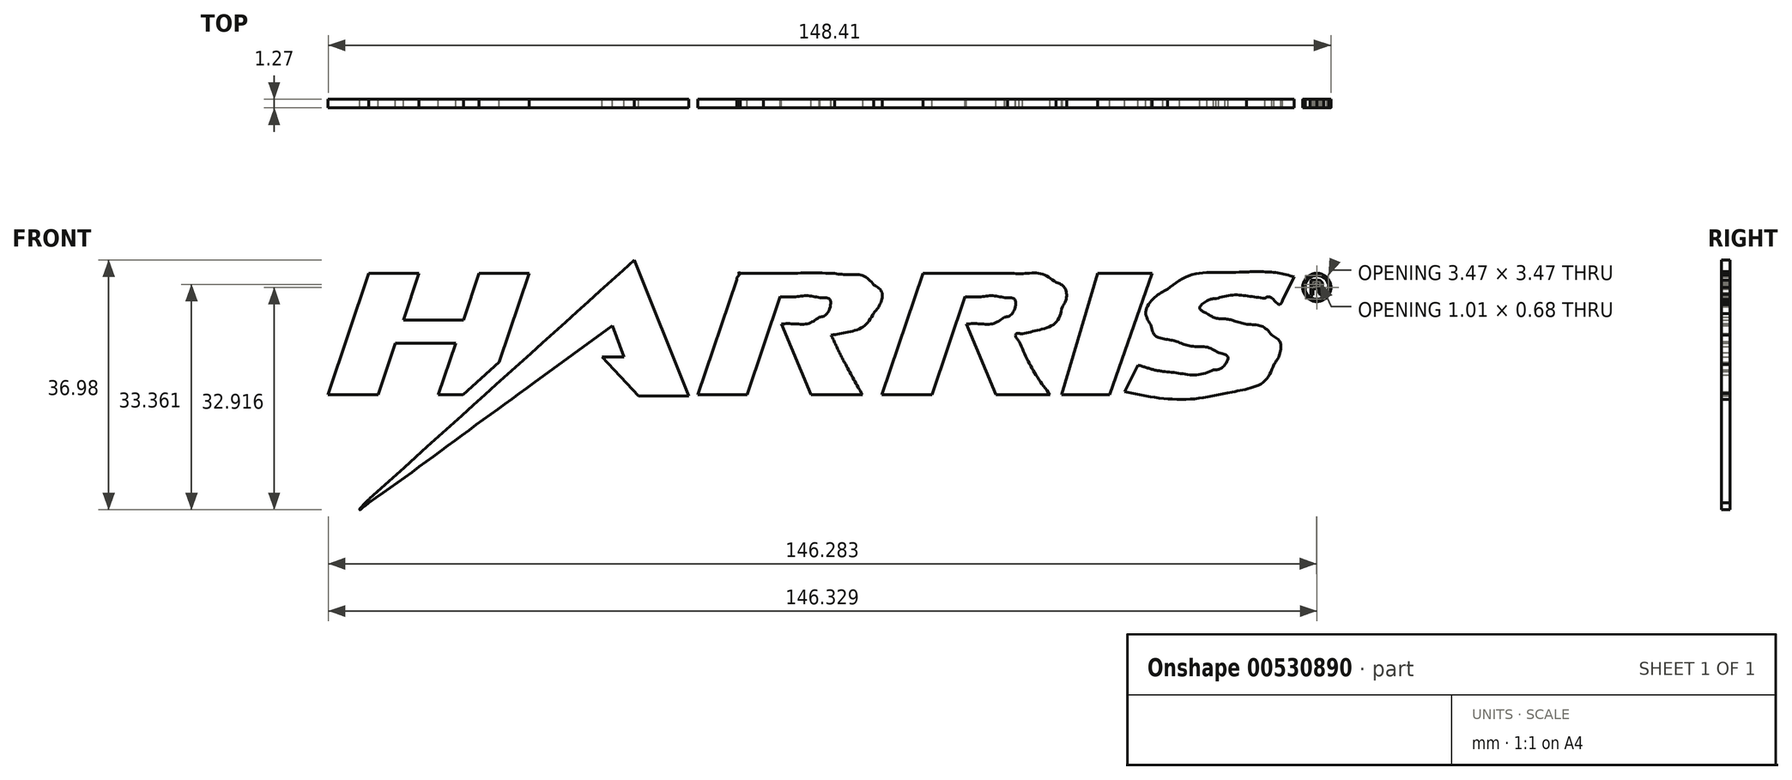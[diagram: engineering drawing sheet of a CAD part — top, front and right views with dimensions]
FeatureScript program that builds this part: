
annotation { "Feature Type Name" : "Feature", "Feature Type Description" : "" }
export const myFeature = defineFeature(function(context is Context, id is Id, definition is map)
    precondition{}
    {
        {
            var Q0;
            Q0=qCreatedBy(makeId("Front.planeOp"),FACE);
            var sketch = newSketch(context, id + "F0", { "sketchPlane" : qUnion([Q0])});
            skFitSpline(sketch, "E0", {"points": [v(63.7, 16.41) * mm, v(59.7, 16.31) * mm, v(55.5, 15.96) * mm, v(52, 13.85) * mm]});
            skFitSpline(sketch, "E1", {"points": [v(52, 13.85) * mm, v(50.3, 12.78) * mm, v(48.82, 10.63) * mm, v(49.53, 8.56) * mm]});
            skFitSpline(sketch, "E2", {"points": [v(49.53, 8.56) * mm, v(50.28, 6.91) * mm, v(52.2, 6.38) * mm, v(53.8, 5.94) * mm]});
            skFitSpline(sketch, "E3", {"points": [v(53.8, 5.94) * mm, v(55.72, 5.38) * mm, v(57.78, 5.29) * mm, v(59.6, 4.42) * mm]});
            skFitSpline(sketch, "E4", {"points": [v(59.6, 4.42) * mm, v(60.96, 3.78) * mm, v(60, 2.15) * mm, v(58.86, 1.94) * mm]});
            skFitSpline(sketch, "E5", {"points": [v(58.86, 1.94) * mm, v(56.44, 1.15) * mm, v(53.82, 1.39) * mm, v(51.33, 1.69) * mm]});
            skFitSpline(sketch, "E6", {"points": [v(51.33, 1.69) * mm, v(50.09, 1.9) * mm, v(48.87, 2.25) * mm, v(47.66, 2.62) * mm]});
            skFitSpline(sketch, "E7", {"points": [v(47.66, 2.62) * mm, v(47, 1.3) * mm, v(46.34, 0) * mm, v(45.68, -1.31) * mm]});
            skFitSpline(sketch, "E8", {"points": [v(45.68, -1.31) * mm, v(50.57, -2.22) * mm, v(55.62, -2.42) * mm, v(60.53, -1.59) * mm]});
            skFitSpline(sketch, "E9", {"points": [v(60.53, -1.59) * mm, v(63.32, -1.03) * mm, v(66.28, 0.15) * mm, v(67.78, 2.72) * mm]});
            skFitSpline(sketch, "E10", {"points": [v(67.78, 2.72) * mm, v(68.57, 4.04) * mm, v(68.7, 5.97) * mm, v(67.46, 7.06) * mm]});
            skFitSpline(sketch, "E11", {"points": [v(67.46, 7.06) * mm, v(65.98, 8.37) * mm, v(63.93, 8.64) * mm, v(62.08, 9.1) * mm]});
            skFitSpline(sketch, "E12", {"points": [v(62.08, 9.1) * mm, v(60.69, 9.44) * mm, v(59.2, 9.56) * mm, v(57.9, 10.22) * mm]});
            skFitSpline(sketch, "E13", {"points": [v(57.9, 10.22) * mm, v(56.8, 11.12) * mm, v(58.22, 12.3) * mm, v(59.2, 12.42) * mm]});
            skFitSpline(sketch, "E14", {"points": [v(59.2, 12.42) * mm, v(61.56, 12.98) * mm, v(64.04, 12.81) * mm, v(66.44, 12.5) * mm]});
            skFitSpline(sketch, "E15", {"points": [v(66.44, 12.5) * mm, v(67.26, 12.67) * mm, v(68.55, 11.58) * mm, v(69.06, 12.18) * mm]});
            skFitSpline(sketch, "E16", {"points": [v(69.06, 12.18) * mm, v(69.63, 13.34) * mm, v(70.2, 14.5) * mm, v(70.78, 15.68) * mm]});
            skFitSpline(sketch, "E17", {"points": [v(70.78, 15.68) * mm, v(68.47, 16.24) * mm, v(66.06, 16.43) * mm, v(63.7, 16.41) * mm]});
            skLineSegment(sketch, "E18", {"start": v(-66.17, 16.22) * mm, "end": v(-72.2, -1.78) * mm});
            skLineSegment(sketch, "E19", {"start": v(-72.2, -1.78) * mm, "end": v(-64.8, -1.78) * mm});
            skLineSegment(sketch, "E20", {"start": v(-64.8, -1.78) * mm, "end": v(-62.24, 5.84) * mm});
            skLineSegment(sketch, "E21", {"start": v(-62.24, 5.84) * mm, "end": v(-53.33, 5.84) * mm});
            skLineSegment(sketch, "E22", {"start": v(-53.33, 5.84) * mm, "end": v(-55.9, -1.78) * mm});
            skLineSegment(sketch, "E23", {"start": v(-55.9, -1.78) * mm, "end": v(-52.23, -1.78) * mm});
            skLineSegment(sketch, "E24", {"start": v(-52.23, -1.78) * mm, "end": v(-46.86, 3.06) * mm});
            skLineSegment(sketch, "E25", {"start": v(-46.86, 3.06) * mm, "end": v(-42.47, 16.22) * mm});
            skLineSegment(sketch, "E26", {"start": v(-42.47, 16.22) * mm, "end": v(-49.87, 16.22) * mm});
            skLineSegment(sketch, "E27", {"start": v(-49.87, 16.22) * mm, "end": v(-52.19, 9.3) * mm});
            skLineSegment(sketch, "E28", {"start": v(-52.19, 9.3) * mm, "end": v(-61.07, 9.3) * mm});
            skLineSegment(sketch, "E29", {"start": v(-61.07, 9.3) * mm, "end": v(-58.75, 16.22) * mm});
            skLineSegment(sketch, "E30", {"start": v(-58.75, 16.22) * mm, "end": v(-66.17, 16.22) * mm});
            skLineSegment(sketch, "E31", {"start": v(-70.17, 16.22) * mm, "end": v(-70.17, 16.22) * mm});
            skFitSpline(sketch, "E32", {"points": [v(4.38, 2.72) * mm, v(3.62, 4.13) * mm, v(2.93, 5.58) * mm, v(2.26, 7.04) * mm]});
            skFitSpline(sketch, "E33", {"points": [v(2.26, 7.04) * mm, v(4.58, 7.47) * mm, v(7.08, 8.34) * mm, v(8.54, 10.31) * mm]});
            skFitSpline(sketch, "E34", {"points": [v(8.54, 10.31) * mm, v(9.42, 11.5) * mm, v(9.75, 13.37) * mm, v(8.57, 14.48) * mm]});
            skFitSpline(sketch, "E35", {"points": [v(8.57, 14.48) * mm, v(6.98, 15.84) * mm, v(4.77, 16) * mm, v(2.78, 16.17) * mm]});
            skFitSpline(sketch, "E36", {"points": [v(2.78, 16.17) * mm, v(-0.74, 16.27) * mm, v(-4.26, 16.2) * mm, v(-7.77, 16.22) * mm]});
            skFitSpline(sketch, "E37", {"points": [v(-7.77, 16.22) * mm, v(-9.03, 16.22) * mm, v(-10.3, 16.22) * mm, v(-11.56, 16.22) * mm]});
            skFitSpline(sketch, "E38", {"points": [v(-11.56, 16.22) * mm, v(-11.19, 16.22) * mm, v(-11.7, 15.53) * mm, v(-11.72, 15.24) * mm]});
            skFitSpline(sketch, "E39", {"points": [v(-11.72, 15.24) * mm, v(-13.64, 9.58) * mm, v(-15.56, 3.9) * mm, v(-17.48, -1.76) * mm]});
            skFitSpline(sketch, "E40", {"points": [v(-17.48, -1.76) * mm, v(-15.05, -1.77) * mm, v(-12.62, -1.77) * mm, v(-10.2, -1.78) * mm]});
            skFitSpline(sketch, "E41", {"points": [v(-10.2, -1.78) * mm, v(-8.57, 3.07) * mm, v(-6.94, 7.9) * mm, v(-5.31, 12.75) * mm]});
            skFitSpline(sketch, "E42", {"points": [v(-5.31, 12.75) * mm, v(-3.35, 12.7) * mm, v(-1.37, 12.88) * mm, v(0.57, 12.56) * mm]});
            skFitSpline(sketch, "E43", {"points": [v(0.57, 12.56) * mm, v(2.09, 12.25) * mm, v(1.6, 10.2) * mm, v(0.48, 9.7) * mm]});
            skFitSpline(sketch, "E44", {"points": [v(0.48, 9.7) * mm, v(-1.22, 8.76) * mm, v(-3.24, 8.72) * mm, v(-5.14, 8.72) * mm]});
            skFitSpline(sketch, "E45", {"points": [v(-5.14, 8.72) * mm, v(-3.68, 5.22) * mm, v(-2.21, 1.72) * mm, v(-0.75, -1.78) * mm]});
            skFitSpline(sketch, "E46", {"points": [v(-0.75, -1.78) * mm, v(1.79, -1.78) * mm, v(4.32, -1.79) * mm, v(6.86, -1.8) * mm]});
            skFitSpline(sketch, "E47", {"points": [v(6.86, -1.8) * mm, v(6.02, -0.3) * mm, v(5.2, 1.2) * mm, v(4.38, 2.72) * mm]});
            skLineSegment(sketch, "E48", {"start": v(4.38, 2.72) * mm, "end": v(4.38, 2.72) * mm});
            skFitSpline(sketch, "E49", {"points": [v(17.2, -1.78) * mm, v(18.82, 3.07) * mm, v(20.45, 7.9) * mm, v(22.08, 12.75) * mm]});
            skFitSpline(sketch, "E50", {"points": [v(22.08, 12.75) * mm, v(24.04, 12.7) * mm, v(26.02, 12.88) * mm, v(27.96, 12.55) * mm]});
            skFitSpline(sketch, "E51", {"points": [v(27.96, 12.55) * mm, v(29.47, 12.26) * mm, v(29.02, 10.2) * mm, v(27.9, 9.7) * mm]});
            skFitSpline(sketch, "E52", {"points": [v(27.9, 9.7) * mm, v(26.19, 8.75) * mm, v(24.15, 8.72) * mm, v(22.25, 8.72) * mm]});
            skFitSpline(sketch, "E53", {"points": [v(22.25, 8.72) * mm, v(23.71, 5.22) * mm, v(25.18, 1.72) * mm, v(26.64, -1.78) * mm]});
            skFitSpline(sketch, "E54", {"points": [v(26.64, -1.78) * mm, v(29.31, -1.78) * mm, v(31.98, -1.78) * mm, v(34.65, -1.78) * mm]});
            skFitSpline(sketch, "E55", {"points": [v(34.65, -1.78) * mm, v(32.86, 0.69) * mm, v(31.33, 3.33) * mm, v(30.08, 6.1) * mm]});
            skFitSpline(sketch, "E56", {"points": [v(30.08, 6.1) * mm, v(29.57, 6.82) * mm, v(29.6, 7.24) * mm, v(30.56, 7.22) * mm]});
            skFitSpline(sketch, "E57", {"points": [v(30.56, 7.22) * mm, v(32.88, 7.8) * mm, v(35.47, 8.89) * mm, v(36.45, 11.25) * mm]});
            skFitSpline(sketch, "E58", {"points": [v(36.45, 11.25) * mm, v(37.05, 12.48) * mm, v(36.74, 14.14) * mm, v(35.5, 14.86) * mm]});
            skFitSpline(sketch, "E59", {"points": [v(35.5, 14.86) * mm, v(33.37, 16.12) * mm, v(30.8, 16.16) * mm, v(28.38, 16.22) * mm]});
            skFitSpline(sketch, "E60", {"points": [v(28.38, 16.22) * mm, v(24.2, 16.22) * mm, v(20.01, 16.22) * mm, v(15.83, 16.22) * mm]});
            skFitSpline(sketch, "E61", {"points": [v(15.83, 16.22) * mm, v(13.8, 10.21) * mm, v(11.77, 4.21) * mm, v(9.74, -1.79) * mm]});
            skFitSpline(sketch, "E62", {"points": [v(9.74, -1.79) * mm, v(12.22, -1.79) * mm, v(14.7, -1.78) * mm, v(17.2, -1.78) * mm]});
            skLineSegment(sketch, "E63", {"start": v(17.2, -1.78) * mm, "end": v(17.2, -1.78) * mm});
            skLineSegment(sketch, "E64", {"start": v(43.49, -1.78) * mm, "end": v(49.76, 16.22) * mm});
            skLineSegment(sketch, "E65", {"start": v(49.76, 16.22) * mm, "end": v(41.68, 16.22) * mm});
            skLineSegment(sketch, "E66", {"start": v(41.68, 16.22) * mm, "end": v(36.35, -1.78) * mm});
            skLineSegment(sketch, "E67", {"start": v(36.35, -1.78) * mm, "end": v(43.49, -1.78) * mm});
            skFitSpline(sketch, "E68", {"points": [v(-26.86, 18.18) * mm, v(-39.92, 6.4) * mm, v(-53, -5.36) * mm, v(-66.04, -17.16) * mm]});
            skFitSpline(sketch, "E69", {"points": [v(-66.04, -17.16) * mm, v(-66.74, -17.83) * mm, v(-67.56, -18.8) * mm, v(-66.22, -17.8) * mm]});
            skFitSpline(sketch, "E70", {"points": [v(-66.22, -17.8) * mm, v(-58.04, -11.95) * mm, v(-49.95, -5.98) * mm, v(-41.8, -0.08) * mm]});
            skFitSpline(sketch, "E71", {"points": [v(-41.8, -0.08) * mm, v(-37.9, 2.76) * mm, v(-34, 5.6) * mm, v(-30.1, 8.43) * mm]});
            skFitSpline(sketch, "E72", {"points": [v(-30.1, 8.43) * mm, v(-29.55, 6.9) * mm, v(-28.99, 5.36) * mm, v(-28.43, 3.82) * mm]});
            skFitSpline(sketch, "E73", {"points": [v(-28.43, 3.82) * mm, v(-29.5, 3.82) * mm, v(-30.57, 3.82) * mm, v(-31.65, 3.82) * mm]});
            skFitSpline(sketch, "E74", {"points": [v(-31.65, 3.82) * mm, v(-29.84, 1.9) * mm, v(-28.04, -0.04) * mm, v(-26.23, -1.97) * mm]});
            skFitSpline(sketch, "E75", {"points": [v(-26.23, -1.97) * mm, v(-23.76, -1.97) * mm, v(-21.3, -1.97) * mm, v(-18.82, -1.97) * mm]});
            skFitSpline(sketch, "E76", {"points": [v(-18.82, -1.97) * mm, v(-21.5, 4.75) * mm, v(-24.18, 11.46) * mm, v(-26.86, 18.18) * mm]});
            skFitSpline(sketch, "E77", {"points": [v(74.13, 16.19) * mm, v(74.48, 16.19) * mm, v(74.82, 16.1) * mm, v(75.15, 15.92) * mm]});
            skFitSpline(sketch, "E78", {"points": [v(75.15, 15.92) * mm, v(75.48, 15.74) * mm, v(75.74, 15.48) * mm, v(75.93, 15.15) * mm]});
            skFitSpline(sketch, "E79", {"points": [v(75.93, 15.15) * mm, v(76.11, 14.82) * mm, v(76.2, 14.47) * mm, v(76.2, 14.11) * mm]});
            skFitSpline(sketch, "E80", {"points": [v(76.2, 14.11) * mm, v(76.2, 13.76) * mm, v(76.11, 13.41) * mm, v(75.93, 13.08) * mm]});
            skFitSpline(sketch, "E81", {"points": [v(75.93, 13.08) * mm, v(75.75, 12.76) * mm, v(75.5, 12.5) * mm, v(75.16, 12.32) * mm]});
            skFitSpline(sketch, "E82", {"points": [v(75.16, 12.32) * mm, v(74.83, 12.14) * mm, v(74.49, 12.04) * mm, v(74.13, 12.04) * mm]});
            skFitSpline(sketch, "E83", {"points": [v(74.13, 12.04) * mm, v(73.77, 12.04) * mm, v(73.43, 12.14) * mm, v(73.1, 12.32) * mm]});
            skFitSpline(sketch, "E84", {"points": [v(73.1, 12.32) * mm, v(72.77, 12.5) * mm, v(72.51, 12.76) * mm, v(72.33, 13.08) * mm]});
            skFitSpline(sketch, "E85", {"points": [v(72.33, 13.08) * mm, v(72.15, 13.41) * mm, v(72.05, 13.76) * mm, v(72.05, 14.11) * mm]});
            skFitSpline(sketch, "E86", {"points": [v(72.05, 14.11) * mm, v(72.05, 14.47) * mm, v(72.15, 14.82) * mm, v(72.34, 15.15) * mm]});
            skFitSpline(sketch, "E87", {"points": [v(72.34, 15.15) * mm, v(72.52, 15.48) * mm, v(72.78, 15.74) * mm, v(73.11, 15.92) * mm]});
            skFitSpline(sketch, "E88", {"points": [v(73.11, 15.92) * mm, v(73.44, 16.1) * mm, v(73.78, 16.19) * mm, v(74.13, 16.19) * mm]});
            skFitSpline(sketch, "E89", {"points": [v(74.13, 15.85) * mm, v(73.84, 15.85) * mm, v(73.55, 15.77) * mm, v(73.28, 15.62) * mm]});
            skFitSpline(sketch, "E90", {"points": [v(73.28, 15.62) * mm, v(73, 15.47) * mm, v(72.79, 15.26) * mm, v(72.63, 14.98) * mm]});
            skFitSpline(sketch, "E91", {"points": [v(72.63, 14.98) * mm, v(72.47, 14.7) * mm, v(72.4, 14.42) * mm, v(72.4, 14.11) * mm]});
            skFitSpline(sketch, "E92", {"points": [v(72.4, 14.11) * mm, v(72.4, 13.81) * mm, v(72.47, 13.53) * mm, v(72.63, 13.25) * mm]});
            skFitSpline(sketch, "E93", {"points": [v(72.63, 13.25) * mm, v(72.78, 12.98) * mm, v(73, 12.77) * mm, v(73.27, 12.62) * mm]});
            skFitSpline(sketch, "E94", {"points": [v(73.27, 12.62) * mm, v(73.55, 12.46) * mm, v(73.83, 12.39) * mm, v(74.13, 12.39) * mm]});
            skFitSpline(sketch, "E95", {"points": [v(74.13, 12.39) * mm, v(74.43, 12.39) * mm, v(74.72, 12.46) * mm, v(75, 12.62) * mm]});
            skFitSpline(sketch, "E96", {"points": [v(75, 12.62) * mm, v(75.27, 12.77) * mm, v(75.48, 12.98) * mm, v(75.63, 13.25) * mm]});
            skFitSpline(sketch, "E97", {"points": [v(75.63, 13.25) * mm, v(75.78, 13.53) * mm, v(75.86, 13.81) * mm, v(75.86, 14.11) * mm]});
            skFitSpline(sketch, "E98", {"points": [v(75.86, 14.11) * mm, v(75.86, 14.42) * mm, v(75.78, 14.7) * mm, v(75.63, 14.98) * mm]});
            skFitSpline(sketch, "E99", {"points": [v(75.63, 14.98) * mm, v(75.47, 15.26) * mm, v(75.26, 15.47) * mm, v(74.98, 15.62) * mm]});
            skFitSpline(sketch, "E100", {"points": [v(74.98, 15.62) * mm, v(74.7, 15.77) * mm, v(74.42, 15.85) * mm, v(74.13, 15.85) * mm]});
            skLineSegment(sketch, "E101", {"start": v(73.22, 12.97) * mm, "end": v(73.22, 15.2) * mm});
            skLineSegment(sketch, "E102", {"start": v(73.22, 15.2) * mm, "end": v(74, 15.2) * mm});
            skFitSpline(sketch, "E103", {"points": [v(74, 15.2) * mm, v(74.25, 15.2) * mm, v(74.45, 15.18) * mm, v(74.56, 15.14) * mm]});
            skFitSpline(sketch, "E104", {"points": [v(74.56, 15.14) * mm, v(74.68, 15.1) * mm, v(74.78, 15.03) * mm, v(74.85, 14.92) * mm]});
            skFitSpline(sketch, "E105", {"points": [v(74.85, 14.92) * mm, v(74.92, 14.82) * mm, v(74.95, 14.7) * mm, v(74.95, 14.6) * mm]});
            skFitSpline(sketch, "E106", {"points": [v(74.95, 14.6) * mm, v(74.95, 14.43) * mm, v(74.9, 14.3) * mm, v(74.78, 14.17) * mm]});
            skFitSpline(sketch, "E107", {"points": [v(74.78, 14.17) * mm, v(74.66, 14.05) * mm, v(74.5, 13.98) * mm, v(74.3, 13.96) * mm]});
            skFitSpline(sketch, "E108", {"points": [v(74.3, 13.96) * mm, v(74.38, 13.93) * mm, v(74.45, 13.89) * mm, v(74.5, 13.85) * mm]});
            skFitSpline(sketch, "E109", {"points": [v(74.5, 13.85) * mm, v(74.58, 13.76) * mm, v(74.7, 13.61) * mm, v(74.83, 13.4) * mm]});
            skLineSegment(sketch, "E110", {"start": v(74.83, 13.4) * mm, "end": v(75.1, 12.97) * mm});
            skLineSegment(sketch, "E111", {"start": v(75.1, 12.97) * mm, "end": v(74.66, 12.97) * mm});
            skLineSegment(sketch, "E112", {"start": v(74.66, 12.97) * mm, "end": v(74.46, 13.32) * mm});
            skFitSpline(sketch, "E113", {"points": [v(74.46, 13.32) * mm, v(74.3, 13.6) * mm, v(74.18, 13.77) * mm, v(74.08, 13.84) * mm]});
            skFitSpline(sketch, "E114", {"points": [v(74.08, 13.84) * mm, v(74.01, 13.89) * mm, v(73.92, 13.92) * mm, v(73.8, 13.92) * mm]});
            skLineSegment(sketch, "E115", {"start": v(73.8, 13.92) * mm, "end": v(73.58, 13.92) * mm});
            skLineSegment(sketch, "E116", {"start": v(73.58, 13.92) * mm, "end": v(73.58, 12.97) * mm});
            skLineSegment(sketch, "E117", {"start": v(73.58, 12.97) * mm, "end": v(73.22, 12.97) * mm});
            skLineSegment(sketch, "E118", {"start": v(73.58, 14.23) * mm, "end": v(74.03, 14.23) * mm});
            skFitSpline(sketch, "E119", {"points": [v(74.03, 14.23) * mm, v(74.24, 14.23) * mm, v(74.39, 14.26) * mm, v(74.47, 14.32) * mm]});
            skFitSpline(sketch, "E120", {"points": [v(74.47, 14.32) * mm, v(74.54, 14.38) * mm, v(74.58, 14.47) * mm, v(74.58, 14.57) * mm]});
            skFitSpline(sketch, "E121", {"points": [v(74.58, 14.57) * mm, v(74.58, 14.63) * mm, v(74.56, 14.7) * mm, v(74.53, 14.74) * mm]});
            skFitSpline(sketch, "E122", {"points": [v(74.53, 14.74) * mm, v(74.49, 14.8) * mm, v(74.44, 14.84) * mm, v(74.37, 14.86) * mm]});
            skFitSpline(sketch, "E123", {"points": [v(74.37, 14.86) * mm, v(74.3, 14.89) * mm, v(74.18, 14.9) * mm, v(74, 14.9) * mm]});
            skLineSegment(sketch, "E124", {"start": v(74, 14.9) * mm, "end": v(73.58, 14.9) * mm});
            skLineSegment(sketch, "E125", {"start": v(73.58, 14.9) * mm, "end": v(73.58, 14.23) * mm});
            skSolve(sketch);
        }
        {
            var Q0;
            Q0 = qSketchRegion(id + "F0", true);
            var Q1;
            Q1=makeQuery(id+"F0.imprint","IMPRINT",FACE,{"disambiguationData":[TD([[makeQuery(id+"F0.imprint","IMPRINT",EDGE,{"derivedFrom":sQuery(id+"F0.wireOp",EDGE,"E101")}),-1.0]])]});
            extrude(context, id + "F1", {"entities" : qUnion([Q0, Q1]), "depth" : 1.27 * mm, "offsetDistance" : 25.4 * mm});
        }
    });
